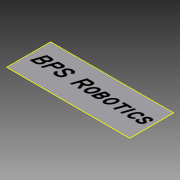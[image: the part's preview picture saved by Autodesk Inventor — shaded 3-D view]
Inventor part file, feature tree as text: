
AUTODESK INVENTOR PART (.ipt)
format: ipt  version: 2014 (Build 180170000, 170)  size: 76,800 bytes
history: native  units: in
note: dims shown in document units (in); Inventor stores cm internally (conversion verified against a paired STEP export)
features: sketch x2, extrude x1
ambient origin geometry x8: Origin, YZ Plane, XZ Plane, XY Plane, X Axis, Y Axis, Z Axis, Center Point
bodies: Solid1 (feature_tree)
feature tree (3):
  extrude  "Extrusion1"  Depth=30.0in
  sketch  "Sketch2"  dims[d2=0.1in d3=0.0in]
  sketch  "Sketch1"  dims[d0=84.0in d1=30.0in]
